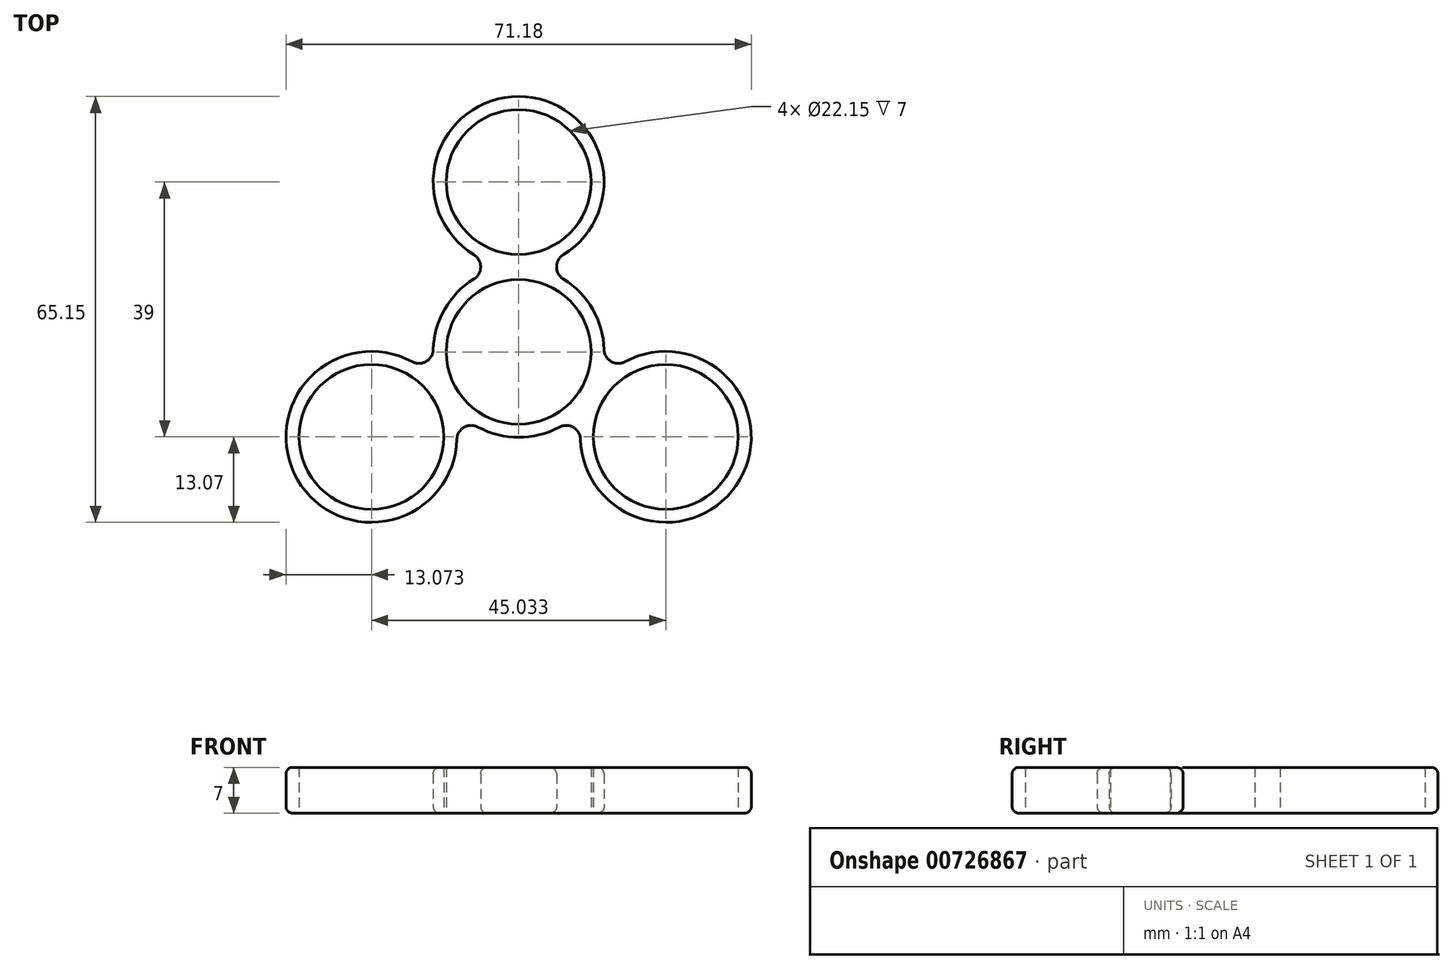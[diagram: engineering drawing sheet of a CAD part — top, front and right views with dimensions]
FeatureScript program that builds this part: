
annotation { "Feature Type Name" : "Feature", "Feature Type Description" : "" }
export const myFeature = defineFeature(function(context is Context, id is Id, definition is map)
    precondition{}
    {
        {
            var Q0;
            Q0=qCreatedBy(makeId("Top.planeOp"),FACE);
            var sketch = newSketch(context, id + "F0", { "sketchPlane" : qUnion([Q0])});
            skCircle(sketch, "E0", {"center": v(0, 0) * mm, "radius": 11.07 * mm});
            skArc(sketch, "E1", {"start": v(-6.85, 11.14) * mm, "mid": v(-11.32, -6.54) * mm, "end": v(6.22, -11.5) * mm});
            skCircle(sketch, "E2", {"center": v(0, 26) * mm, "radius": 11.07 * mm});
            skArc(sketch, "E3", {"start": v(6.85, 14.86) * mm, "mid": v(0, 39.07) * mm, "end": v(-6.85, 14.86) * mm});
            skLineSegment(sketch, "E4", {"start": v(0, 26) * mm, "end": v(0, 0) * mm, "construction": true});
            skPoint(sketch, "E5", {"position": v(0, 13) * mm});
            skArc(sketch, "E6", {"start": v(-6.85, 11.14) * mm, "mid": v(-5.81, 13) * mm, "end": v(-6.85, 14.86) * mm});
            skArc(sketch, "E7.MirrorC", {"start": v(6.85, 11.14) * mm, "mid": v(5.81, 13) * mm, "end": v(6.85, 14.86) * mm});
            skLineSegment(sketch, "E8", {"start": v(-8, 13) * mm, "end": v(8, 13) * mm, "construction": true});
            skArc(sketch, "E9.1.0", {"start": v(-16.3, -1.5) * mm, "mid": v(-33.84, -19.54) * mm, "end": v(-9.45, -13.37) * mm});
            skCircle(sketch, "E9.1.1", {"center": v(-22.52, -13) * mm, "radius": 11.07 * mm});
            skArc(sketch, "E9.1.2", {"start": v(-13.07, 0.37) * mm, "mid": v(-14.16, -1.47) * mm, "end": v(-16.3, -1.5) * mm});
            skArc(sketch, "E9.1.3", {"start": v(-6.22, -11.5) * mm, "mid": v(-8.35, -11.53) * mm, "end": v(-9.45, -13.37) * mm});
            skArc(sketch, "E10.trimOffspring", {"start": v(13.07, 0.37) * mm, "mid": v(-11.32, 6.54) * mm, "end": v(6.22, -11.5) * mm});
            skArc(sketch, "E11.trimOffspring", {"start": v(13.07, 0.37) * mm, "mid": v(11.32, 6.54) * mm, "end": v(6.85, 11.14) * mm});
            skArc(sketch, "E12.3.2.0", {"start": v(9.45, -13.37) * mm, "mid": v(33.84, -19.54) * mm, "end": v(16.3, -1.5) * mm});
            skCircle(sketch, "E12.4.2.0", {"center": v(22.52, -13) * mm, "radius": 11.07 * mm});
            skArc(sketch, "E12.6.2.0", {"start": v(6.22, -11.5) * mm, "mid": v(8.35, -11.53) * mm, "end": v(9.45, -13.37) * mm});
            skArc(sketch, "E12.10.2.0", {"start": v(13.07, 0.37) * mm, "mid": v(14.16, -1.47) * mm, "end": v(16.3, -1.5) * mm});
            skSolve(sketch);
        }
        {
            var Q0;
            Q0 = qSketchRegion(id + "F0", true);
            extrude(context, id + "F1", {"entities" : qUnion([Q0]), "endBound" : BoundingType.SYMMETRIC, "depth" : 7 * mm, "offsetDistance" : 25 * mm});
        }
        {
            var Q0;
            Q0=makeQuery(id+"F1.opExtrude","CAP_EDGE",EDGE,{"disambiguationData":[OSD([sQuery(id+"F0.wireOp",EDGE,"E9.1.2")])],"isStart":false});
            var Q1;
            Q1=makeQuery(id+"F1.opExtrude","CAP_EDGE",EDGE,{"disambiguationData":[OSD([sQuery(id+"F0.wireOp",EDGE,"E7.MirrorC")])],"isStart":true});
            var Q2;
            Q2=makeQuery(id+"F1.opExtrude","CAP_EDGE",EDGE,{"disambiguationData":[OSD([sQuery(id+"F0.wireOp",EDGE,"E6")])],"isStart":false});
            var Q3;
            Q3=makeQuery(id+"F1.opExtrude","CAP_EDGE",EDGE,{"disambiguationData":[OSD([sQuery(id+"F0.wireOp",EDGE,"1829b2bc-9344-4242-9ae7-2c6c3dcbbc50.6.2.0")])],"isStart":false});
            var Q4;
            Q4=makeQuery(id+"F1.opExtrude","CAP_EDGE",EDGE,{"disambiguationData":[OSD([sQuery(id+"F0.wireOp",EDGE,"E9.1.3")])],"isStart":false});
            var Q5;
            Q5=makeQuery(id+"F1.opExtrude","CAP_EDGE",EDGE,{"disambiguationData":[OSD([sQuery(id+"F0.wireOp",EDGE,"1829b2bc-9344-4242-9ae7-2c6c3dcbbc50.10.2.0")])],"isStart":false});
            var Q6;
            Q6=makeQuery(id+"F1.opExtrude","CAP_EDGE",EDGE,{"disambiguationData":[OSD([sQuery(id+"F0.wireOp",EDGE,"1829b2bc-9344-4242-9ae7-2c6c3dcbbc50.6.3.0")])],"isStart":false});
            var Q7;
            Q7=makeQuery(id+"F1.opExtrude","CAP_EDGE",EDGE,{"disambiguationData":[OSD([sQuery(id+"F0.wireOp",EDGE,"1829b2bc-9344-4242-9ae7-2c6c3dcbbc50.10.3.0")])],"isStart":false});
            var Q8;
            Q8=makeQuery(id+"F1.opExtrude","CAP_EDGE",EDGE,{"disambiguationData":[OSD([sQuery(id+"F0.wireOp",EDGE,"E7.MirrorC")])],"isStart":false});
            var Q9;
            Q9=makeQuery(id+"F1.opExtrude","CAP_EDGE",EDGE,{"disambiguationData":[OSD([sQuery(id+"F0.wireOp",EDGE,"1829b2bc-9344-4242-9ae7-2c6c3dcbbc50.6.3.0")])],"isStart":true});
            var Q10;
            Q10=makeQuery(id+"F1.opExtrude","CAP_EDGE",EDGE,{"disambiguationData":[OSD([sQuery(id+"F0.wireOp",EDGE,"1829b2bc-9344-4242-9ae7-2c6c3dcbbc50.10.2.0")])],"isStart":true});
            var Q11;
            Q11=makeQuery(id+"F1.opExtrude","CAP_EDGE",EDGE,{"disambiguationData":[OSD([sQuery(id+"F0.wireOp",EDGE,"1829b2bc-9344-4242-9ae7-2c6c3dcbbc50.10.3.0")])],"isStart":true});
            var Q12;
            Q12=makeQuery(id+"F1.opExtrude","CAP_EDGE",EDGE,{"disambiguationData":[OSD([sQuery(id+"F0.wireOp",EDGE,"E6")])],"isStart":true});
            var Q13;
            Q13=makeQuery(id+"F1.opExtrude","CAP_EDGE",EDGE,{"disambiguationData":[OSD([sQuery(id+"F0.wireOp",EDGE,"E9.1.2")])],"isStart":true});
            var Q14;
            Q14=makeQuery(id+"F1.opExtrude","CAP_EDGE",EDGE,{"disambiguationData":[OSD([sQuery(id+"F0.wireOp",EDGE,"E9.1.3")])],"isStart":true});
            var Q15;
            Q15=makeQuery(id+"F1.opExtrude","CAP_EDGE",EDGE,{"disambiguationData":[OSD([sQuery(id+"F0.wireOp",EDGE,"1829b2bc-9344-4242-9ae7-2c6c3dcbbc50.6.2.0")])],"isStart":true});
            fillet(context, id + "F2", {"entities" : qUnion([Q0, Q1, Q2, Q3, Q4, Q5, Q6, Q7, Q8, Q9, Q10, Q11, Q12, Q13, Q14, Q15]), "radius" : 1 * mm, "tangentPropagation" : true, "allowEdgeOverflow" : false});
        }
    });
